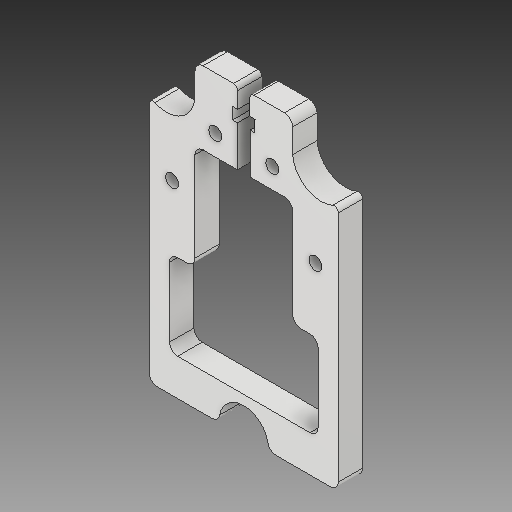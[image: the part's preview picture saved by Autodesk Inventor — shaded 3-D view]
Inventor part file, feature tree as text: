
AUTODESK INVENTOR PART (.ipt)
format: ipt  version: 2017 (Build 210142000, 142)  size: 193,024 bytes
history: native  units: mm
features: other x3, sketch x2
ambient origin geometry x8: Origin, YZ Plane, XZ Plane, XY Plane, X Axis, Y Axis, Z Axis, Center Point
bodies: Solid1 (feature_tree)
feature tree (5):
  other  "Hotend Slide Part 2.ipt"
  other  "Solid1::Hotend Slide Part 2.ipt"
  other  "TaggingFeature1"
  sketch  "Sketch1"  dims[d0=10.0mm]
  sketch  "Sketch2"
